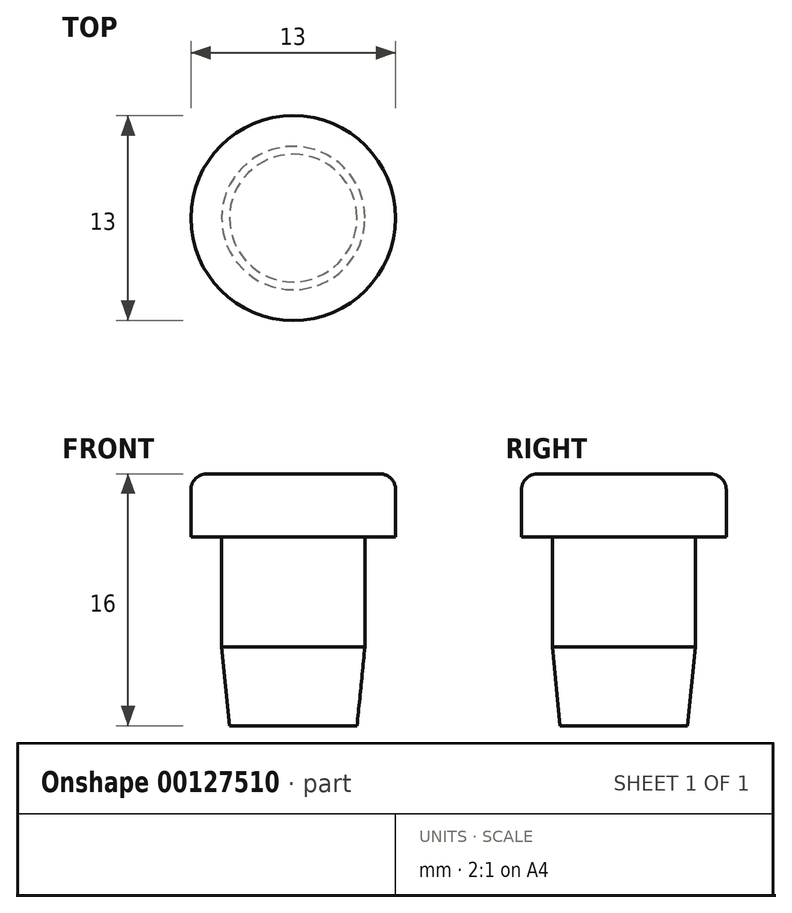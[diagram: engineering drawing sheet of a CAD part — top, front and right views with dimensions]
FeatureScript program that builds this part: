
annotation { "Feature Type Name" : "Feature", "Feature Type Description" : "" }
export const myFeature = defineFeature(function(context is Context, id is Id, definition is map)
    precondition{}
    {
        {
            var Q0;
            Q0=qCreatedBy(makeId("Top.planeOp"),FACE);
            var sketch = newSketch(context, id + "F0", { "sketchPlane" : qUnion([Q0])});
            skCircle(sketch, "E0", {"center": v(0, 0) * mm, "radius": 4.55 * mm});
            skSolve(sketch);
        }
        {
            var Q0;
            Q0 = qSketchRegion(id + "F0", true);
            extrude(context, id + "F1", {"entities" : qUnion([Q0]), "depth" : 12 * mm});
        }
        {
            var Q0;
            Q0=makeQuery(id+"F1.opExtrude","CAP_EDGE",EDGE,{"disambiguationData":[OSD([sQuery(id+"F0.wireOp",EDGE,"E0")])],"isStart":true});
            chamfer(context, id + "F2", {"entities" : qUnion([Q0]), "chamferType" : ChamferType.TWO_OFFSETS, "width1" : 5 * mm, "oppositeDirection" : false, "width2" : .5 * mm, "tangentPropagation" : true});
        }
        {
            var Q0;
            Q0=makeQuery(id+"F1.opExtrude","CAP_FACE",FACE,{"disambiguationData":[OSD([sQuery(id+"F0.wireOp",EDGE,"E0")])],"isStart":false});
            var sketch = newSketch(context, id + "F3", { "sketchPlane" : qUnion([Q0])});
            skCircle(sketch, "E1", {"center": v(0, 0) * mm, "radius": 6.5 * mm});
            skSolve(sketch);
        }
        {
            var Q0;
            Q0=makeQuery(id+"F3.imprint","IMPRINT",FACE,{"disambiguationData":[TD([[makeQuery(id+"F3.imprint","IMPRINT",EDGE,{"derivedFrom":sQuery(id+"F3.wireOp",EDGE,"E1")}),1.0]])]});
            var Q1;
            Q1=makeQuery(id+"F3.imprint","IMPRINT",FACE,{"disambiguationData":[TD([[makeQuery(id+"F3.imprint","IMPRINT",EDGE,{"derivedFrom":sQuery(id+"F3.wireOp",EDGE,"E1")}),1.0]])]});
            var Q2;
            Q2=makeQuery(id+"F3.imprint","IMPRINT",FACE,{"disambiguationData":[TD([[makeQuery(id+"F3.imprint","IMPRINT",EDGE,{"derivedFrom":makeQuery(id+"F1.opExtrude","CAP_EDGE",EDGE,{"disambiguationData":[OSD([sQuery(id+"F0.wireOp",EDGE,"E0")])],"isStart":false})}),1.0]])]});
            extrude(context, id + "F4", {"entities" : qUnion([Q0, Q1, Q2]), "operationType" : NewBodyOperationType.ADD, "depth" : 4 * mm});
        }
        {
            var Q0;
            Q0=makeQuery(id+"F4.opExtrude","CAP_EDGE",EDGE,{"disambiguationData":[OSD([sQuery(id+"F3.wireOp",EDGE,"E1")])],"isStart":false});
            fillet(context, id + "F5", {"entities" : qUnion([Q0]), "radius" : 1 * mm, "tangentPropagation" : true, "allowEdgeOverflow" : false});
        }
    });
